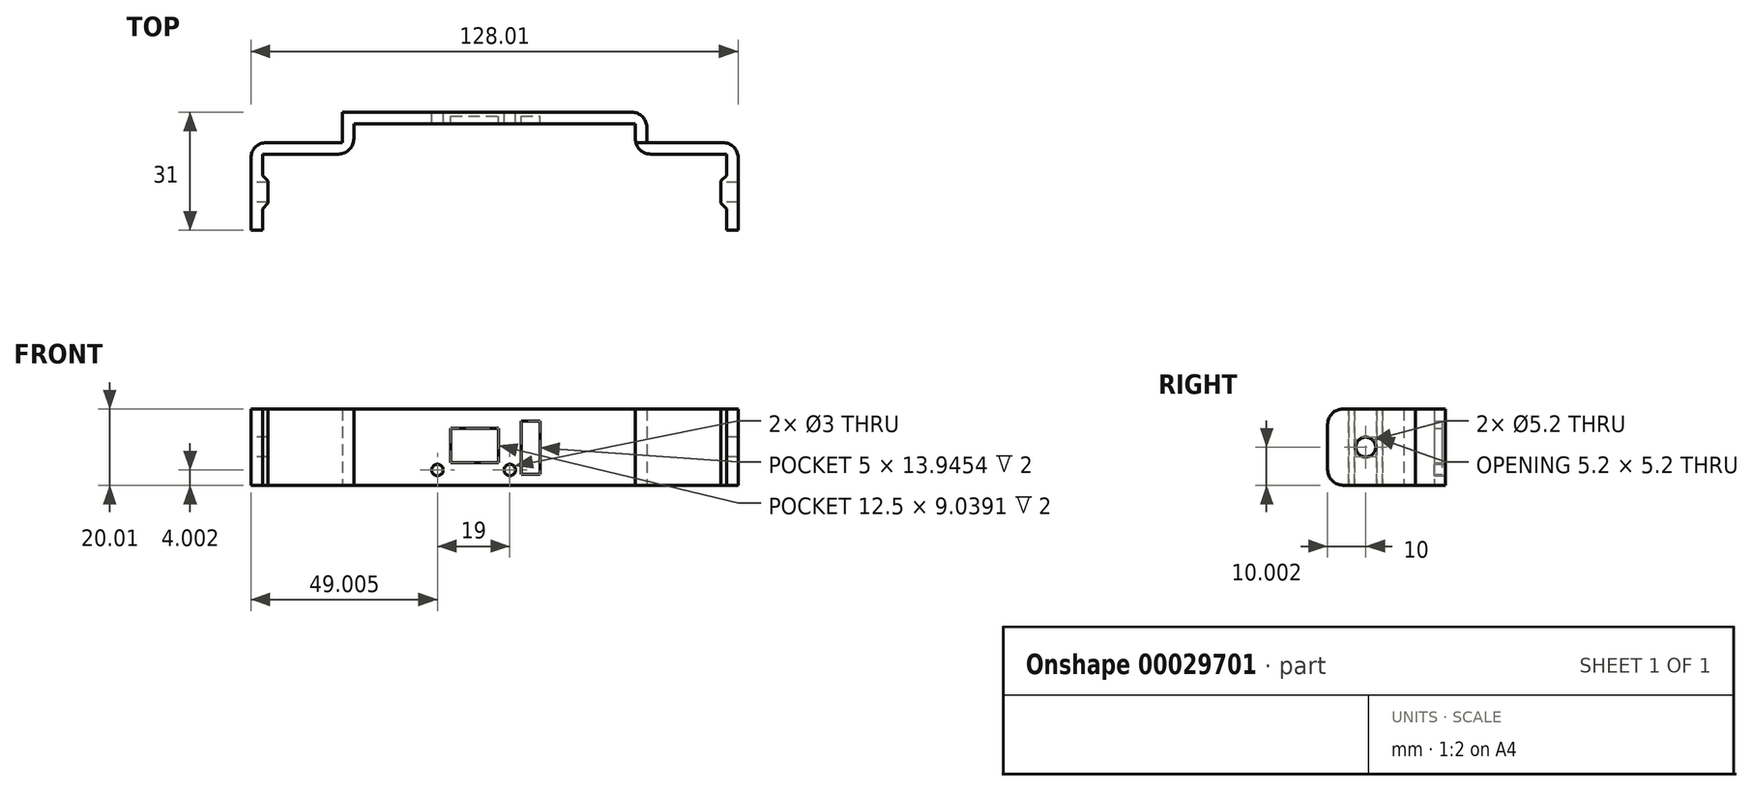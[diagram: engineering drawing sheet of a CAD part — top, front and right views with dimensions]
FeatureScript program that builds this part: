
annotation { "Feature Type Name" : "Feature", "Feature Type Description" : "" }
export const myFeature = defineFeature(function(context is Context, id is Id, definition is map)
    precondition{}
    {
        {
            var Q0;
            Q0=qCreatedBy(makeId("Front.planeOp"),FACE);
            var sketch = newSketch(context, id + "F0", { "sketchPlane" : qUnion([Q0])});
            skLineSegment(sketch, "E0.bottom", {"start": v(-55.19, 32.47) * mm, "end": v(24.81, 32.47) * mm});
            skLineSegment(sketch, "E0.top", {"start": v(-55.19, 12.47) * mm, "end": v(24.81, 12.47) * mm});
            skLineSegment(sketch, "E0.left", {"start": v(-55.19, 32.47) * mm, "end": v(-55.19, 12.47) * mm});
            skLineSegment(sketch, "E0.right", {"start": v(24.81, 32.47) * mm, "end": v(24.81, 12.47) * mm});
            skLineSegment(sketch, "E1.bottom", {"start": v(-26.69, 27.47) * mm, "end": v(-14.19, 27.47) * mm});
            skLineSegment(sketch, "E1.top", {"start": v(-26.69, 18.43) * mm, "end": v(-14.19, 18.43) * mm});
            skLineSegment(sketch, "E1.left", {"start": v(-26.69, 27.47) * mm, "end": v(-26.69, 18.43) * mm});
            skLineSegment(sketch, "E1.right", {"start": v(-14.19, 27.47) * mm, "end": v(-14.19, 18.43) * mm});
            skLineSegment(sketch, "E2.bottom", {"start": v(-8.19, 29.27) * mm, "end": v(-3.19, 29.27) * mm});
            skLineSegment(sketch, "E2.top", {"start": v(-8.19, 15.33) * mm, "end": v(-3.19, 15.33) * mm});
            skLineSegment(sketch, "E2.left", {"start": v(-8.19, 29.27) * mm, "end": v(-8.19, 15.33) * mm});
            skLineSegment(sketch, "E2.right", {"start": v(-3.19, 29.27) * mm, "end": v(-3.19, 15.33) * mm});
            skLineSegment(sketch, "E3.left", {"start": v(-55.19, 32.47) * mm, "end": v(-55.19, 29.47) * mm});
            skLineSegment(sketch, "E3.right", {"start": v(24.81, 32.47) * mm, "end": v(24.81, 29.47) * mm});
            skCircle(sketch, "E4", {"center": v(-30.19, 16.47) * mm, "radius": 1.5 * mm});
            skCircle(sketch, "E5", {"center": v(-11.19, 16.47) * mm, "radius": 1.5 * mm});
            skLineSegment(sketch, "E6.bottom", {"start": v(-55.19, 12.47) * mm, "end": v(-52.19, 12.47) * mm});
            skLineSegment(sketch, "E6.top", {"start": v(-55.19, 32.47) * mm, "end": v(-52.19, 32.47) * mm});
            skLineSegment(sketch, "E6.left", {"start": v(-55.19, 12.47) * mm, "end": v(-55.19, 32.47) * mm});
            skSolve(sketch);
        }
        {
            var Q0;
            Q0=makeQuery(id+"F0.imprint","IMPRINT",FACE,{"disambiguationData":[TD([[makeQuery(id+"F0.imprint","IMPRINT",EDGE,{"derivedFrom":sQuery(id+"F0.wireOp",EDGE,"E2.bottom")}),-1.0]])]});
            var Q1;
            Q1=makeQuery(id+"F0.imprint","IMPRINT",FACE,{"disambiguationData":[TD([[makeQuery(id+"F0.imprint","IMPRINT",EDGE,{"derivedFrom":sQuery(id+"F0.wireOp",EDGE,"E1.bottom")}),-1.0]])]});
            extrude(context, id + "F1", {"entities" : qUnion([Q0, Q1]), "depth" : 1 * mm});
        }
        {
            var Q0;
            Q0 = qSketchRegion(id + "F0", true);
            extrude(context, id + "F2", {"entities" : qUnion([Q0]), "operationType" : NewBodyOperationType.ADD, "depth" : 3 * mm});
        }
        {
            var Q0;
            Q0=makeQuery(id+"F2.opExtrude","CAP_FACE",FACE,{"disambiguationData":[OSD([sQuery(id+"F0.wireOp",EDGE,"E0.top"),sQuery(id+"F0.wireOp",EDGE,"E0.right"),sQuery(id+"F0.wireOp",EDGE,"E1.bottom"),sQuery(id+"F0.wireOp",EDGE,"E1.top"),sQuery(id+"F0.wireOp",EDGE,"E1.left"),sQuery(id+"F0.wireOp",EDGE,"E1.right"),sQuery(id+"F0.wireOp",EDGE,"E2.bottom"),sQuery(id+"F0.wireOp",EDGE,"E2.top"),sQuery(id+"F0.wireOp",EDGE,"E2.left"),sQuery(id+"F0.wireOp",EDGE,"E2.right"),sQuery(id+"F0.wireOp",EDGE,"E0.bottom"),sQuery(id+"F0.wireOp",EDGE,"E3.right"),sQuery(id+"F0.wireOp",EDGE,"E4"),sQuery(id+"F0.wireOp",EDGE,"E5"),sQuery(id+"F0.wireOp",EDGE,"E6.bottom"),sQuery(id+"F0.wireOp",EDGE,"E6.top"),sQuery(id+"F0.wireOp",EDGE,"E6.left")])],"isStart":false});
            var sketch = newSketch(context, id + "F3", { "sketchPlane" : qUnion([Q0])});
            skLineSegment(sketch, "E7.bottom", {"start": v(-55.19, 32.47) * mm, "end": v(-52.19, 32.47) * mm});
            skLineSegment(sketch, "E7.top", {"start": v(-55.19, 12.47) * mm, "end": v(-52.19, 12.47) * mm});
            skLineSegment(sketch, "E7.left", {"start": v(-55.19, 32.47) * mm, "end": v(-55.19, 12.47) * mm});
            skLineSegment(sketch, "E7.right", {"start": v(-52.19, 32.47) * mm, "end": v(-52.19, 12.47) * mm});
            skLineSegment(sketch, "E8.bottom", {"start": v(24.81, 32.47) * mm, "end": v(21.81, 32.47) * mm});
            skLineSegment(sketch, "E8.top", {"start": v(24.81, 12.47) * mm, "end": v(21.81, 12.47) * mm});
            skLineSegment(sketch, "E8.left", {"start": v(24.81, 32.47) * mm, "end": v(24.81, 12.47) * mm});
            skLineSegment(sketch, "E8.right", {"start": v(21.81, 32.47) * mm, "end": v(21.81, 12.47) * mm});
            skSolve(sketch);
        }
        {
            var Q0;
            Q0 = qSketchRegion(id + "F3", true);
            extrude(context, id + "F4", {"entities" : qUnion([Q0]), "operationType" : NewBodyOperationType.ADD, "depth" : 5 * mm});
        }
        {
            var Q0;
            Q0=makeQuery(id+"F4.opExtrude","CAP_FACE",FACE,{"disambiguationData":[OSD([sQuery(id+"F3.wireOp",EDGE,"E7.bottom"),sQuery(id+"F3.wireOp",EDGE,"E7.top"),sQuery(id+"F3.wireOp",EDGE,"E7.left"),sQuery(id+"F3.wireOp",EDGE,"E7.right")])],"isStart":false});
            var sketch = newSketch(context, id + "F5", { "sketchPlane" : qUnion([Q0])});
            skLineSegment(sketch, "E9.bottom", {"start": v(-52.19, 32.47) * mm, "end": v(-79.19, 32.47) * mm});
            skLineSegment(sketch, "E9.top", {"start": v(-52.19, 12.47) * mm, "end": v(-79.19, 12.47) * mm});
            skLineSegment(sketch, "E9.left", {"start": v(-52.19, 32.47) * mm, "end": v(-52.19, 12.47) * mm});
            skLineSegment(sketch, "E9.right", {"start": v(-79.19, 32.47) * mm, "end": v(-79.19, 12.47) * mm});
            skLineSegment(sketch, "E10.bottom", {"start": v(21.82, 32.48) * mm, "end": v(48.82, 32.48) * mm});
            skLineSegment(sketch, "E10.top", {"start": v(21.82, 12.47) * mm, "end": v(48.82, 12.47) * mm});
            skLineSegment(sketch, "E10.left", {"start": v(21.82, 32.48) * mm, "end": v(21.82, 12.47) * mm});
            skLineSegment(sketch, "E10.right", {"start": v(48.82, 32.48) * mm, "end": v(48.82, 12.47) * mm});
            skSolve(sketch);
        }
        {
            var Q0;
            Q0 = qSketchRegion(id + "F5", true);
            extrude(context, id + "F6", {"entities" : qUnion([Q0]), "operationType" : NewBodyOperationType.ADD, "depth" : 3 * mm});
        }
        {
            var Q0;
            Q0=makeQuery(id+"F6.opExtrude","CAP_FACE",FACE,{"disambiguationData":[OSD([sQuery(id+"F5.wireOp",EDGE,"E9.bottom"),sQuery(id+"F5.wireOp",EDGE,"E9.top"),sQuery(id+"F5.wireOp",EDGE,"E9.left"),sQuery(id+"F5.wireOp",EDGE,"E9.right")])],"isStart":false});
            var sketch = newSketch(context, id + "F7", { "sketchPlane" : qUnion([Q0])});
            skLineSegment(sketch, "E11.bottom", {"start": v(-79.19, 32.47) * mm, "end": v(-76.19, 32.47) * mm});
            skLineSegment(sketch, "E11.top", {"start": v(-79.19, 12.47) * mm, "end": v(-76.19, 12.47) * mm});
            skLineSegment(sketch, "E11.left", {"start": v(-79.19, 32.47) * mm, "end": v(-79.19, 12.47) * mm});
            skLineSegment(sketch, "E11.right", {"start": v(-76.19, 32.47) * mm, "end": v(-76.19, 12.47) * mm});
            skSolve(sketch);
        }
        {
            var Q0;
            Q0 = qSketchRegion(id + "F7", true);
            extrude(context, id + "F8", {"entities" : qUnion([Q0]), "operationType" : NewBodyOperationType.ADD, "depth" : 20 * mm});
        }
        {
            var Q0;
            Q0=makeQuery(id+"F6.opExtrude","CAP_FACE",FACE,{"disambiguationData":[OSD([sQuery(id+"F5.wireOp",EDGE,"E10.bottom"),sQuery(id+"F5.wireOp",EDGE,"E10.top"),sQuery(id+"F5.wireOp",EDGE,"E10.left"),sQuery(id+"F5.wireOp",EDGE,"E10.right")])],"isStart":false});
            var sketch = newSketch(context, id + "F9", { "sketchPlane" : qUnion([Q0])});
            skLineSegment(sketch, "E12.bottom", {"start": v(48.82, 32.48) * mm, "end": v(45.82, 32.48) * mm});
            skLineSegment(sketch, "E12.top", {"start": v(48.82, 12.47) * mm, "end": v(45.82, 12.47) * mm});
            skLineSegment(sketch, "E12.left", {"start": v(48.82, 32.48) * mm, "end": v(48.82, 12.47) * mm});
            skLineSegment(sketch, "E12.right", {"start": v(45.82, 32.48) * mm, "end": v(45.82, 12.47) * mm});
            skSolve(sketch);
        }
        {
            var Q0;
            Q0 = qSketchRegion(id + "F9", true);
            extrude(context, id + "F10", {"entities" : qUnion([Q0]), "operationType" : NewBodyOperationType.ADD, "depth" : 20 * mm});
        }
        {
            var Q0;
            Q0=makeQuery(id+"F10.opExtrude","SWEPT_FACE",FACE,{"disambiguationData":[OSD([sQuery(id+"F9.wireOp",EDGE,"E12.right")])]});
            var sketch = newSketch(context, id + "F11", { "sketchPlane" : qUnion([Q0])});
            skLineSegment(sketch, "E13.bottom", {"start": v(25.4, 32.48) * mm, "end": v(16.6, 32.48) * mm});
            skLineSegment(sketch, "E13.top", {"start": v(25.4, 12.47) * mm, "end": v(16.6, 12.47) * mm});
            skLineSegment(sketch, "E13.left", {"start": v(25.4, 32.48) * mm, "end": v(25.4, 12.47) * mm});
            skLineSegment(sketch, "E13.right", {"start": v(16.6, 32.48) * mm, "end": v(16.6, 12.47) * mm});
            skSolve(sketch);
        }
        {
            var Q0;
            Q0=makeQuery(id+"F8.opExtrude","SWEPT_FACE",FACE,{"disambiguationData":[OSD([sQuery(id+"F7.wireOp",EDGE,"E11.right")])]});
            var sketch = newSketch(context, id + "F12", { "sketchPlane" : qUnion([Q0])});
            skLineSegment(sketch, "E14.bottom", {"start": v(-25.4, 12.47) * mm, "end": v(-16.6, 12.47) * mm});
            skLineSegment(sketch, "E14.top", {"start": v(-25.4, 32.47) * mm, "end": v(-16.6, 32.47) * mm});
            skLineSegment(sketch, "E14.left", {"start": v(-25.4, 12.47) * mm, "end": v(-25.4, 32.47) * mm});
            skLineSegment(sketch, "E14.right", {"start": v(-16.6, 12.47) * mm, "end": v(-16.6, 32.47) * mm});
            skSolve(sketch);
        }
        {
            var Q0;
            Q0 = qSketchRegion(id + "F12", true);
            extrude(context, id + "F13", {"entities" : qUnion([Q0]), "operationType" : NewBodyOperationType.ADD, "depth" : 1.5 * mm});
        }
        {
            var Q0;
            Q0 = qSketchRegion(id + "F11", true);
            extrude(context, id + "F14", {"entities" : qUnion([Q0]), "operationType" : NewBodyOperationType.ADD, "depth" : 1.5 * mm});
        }
        {
            var Q0;
            Q0=makeQuery(id+"F8.boolean.opBoolean","MERGE",FACE,{"derivedFrom":[makeQuery(id+"F6.opExtrude","SWEPT_FACE",FACE,{"disambiguationData":[OSD([sQuery(id+"F5.wireOp",EDGE,"E9.right")])]}),makeQuery(id+"F8.opExtrude","SWEPT_FACE",FACE,{"disambiguationData":[OSD([sQuery(id+"F7.wireOp",EDGE,"E11.left")])]})]});
            var sketch = newSketch(context, id + "F15", { "sketchPlane" : qUnion([Q0])});
            skCircle(sketch, "E15", {"center": v(21, 22.47) * mm, "radius": 2.6 * mm});
            skSolve(sketch);
        }
        {
            var Q0;
            Q0=makeQuery(id+"F15.imprint","IMPRINT",FACE,{"disambiguationData":[TD([[makeQuery(id+"F15.imprint","IMPRINT",EDGE,{"derivedFrom":sQuery(id+"F15.wireOp",EDGE,"E15")}),1.0]])]});
            extrude(context, id + "F16", {"entities" : qUnion([Q0]), "operationType" : NewBodyOperationType.REMOVE, "endBound" : BoundingType.THROUGH_ALL, "oppositeDirection" : true, "depth" : 25 * mm});
        }
        {
            var Q0;
            Q0=makeQuery(id+"F8.opExtrude","CAP_EDGE",EDGE,{"disambiguationData":[OSD([sQuery(id+"F7.wireOp",EDGE,"E11.bottom")])],"isStart":false});
            var Q1;
            Q1=makeQuery(id+"F10.opExtrude","CAP_EDGE",EDGE,{"disambiguationData":[OSD([sQuery(id+"F9.wireOp",EDGE,"E12.bottom")])],"isStart":false});
            var Q2;
            Q2=makeQuery(id+"F8.opExtrude","CAP_EDGE",EDGE,{"disambiguationData":[OSD([sQuery(id+"F7.wireOp",EDGE,"E11.top")])],"isStart":false});
            var Q3;
            Q3=makeQuery(id+"F10.opExtrude","CAP_EDGE",EDGE,{"disambiguationData":[OSD([sQuery(id+"F9.wireOp",EDGE,"E12.top")])],"isStart":false});
            var Q4;
            Q4=makeQuery(id+"F4.opExtrude","CAP_EDGE",EDGE,{"disambiguationData":[OSD([sQuery(id+"F3.wireOp",EDGE,"E8.right")])],"isStart":true});
            var Q5;
            Q5=makeQuery(id+"F4.opExtrude","CAP_EDGE",EDGE,{"disambiguationData":[OSD([sQuery(id+"F3.wireOp",EDGE,"E7.right")])],"isStart":true});
            var Q6;
            Q6=makeQuery(id+"F2.opExtrude","CAP_EDGE",EDGE,{"disambiguationData":[OSD([sQuery(id+"F0.wireOp",EDGE,"E6.left")])],"isStart":true});
            var Q7;
            Q7=makeQuery(id+"F2.opExtrude","CAP_EDGE",EDGE,{"disambiguationData":[OSD([sQuery(id+"F0.wireOp",EDGE,"E0.right"),sQuery(id+"F0.wireOp",EDGE,"E3.right")])],"isStart":true});
            var Q8;
            Q8=makeQuery(id+"F6.opExtrude","CAP_EDGE",EDGE,{"disambiguationData":[OSD([sQuery(id+"F5.wireOp",EDGE,"E10.left")])],"isStart":false});
            var Q9;
            Q9=makeQuery(id+"F4.opExtrude","CAP_EDGE",EDGE,{"disambiguationData":[OSD([sQuery(id+"F3.wireOp",EDGE,"E8.left")])],"isStart":false});
            var Q10;
            Q10=makeQuery(id+"F6.opExtrude","CAP_EDGE",EDGE,{"disambiguationData":[OSD([sQuery(id+"F5.wireOp",EDGE,"E10.right")])],"isStart":true});
            var Q11;
            Q11=makeQuery(id+"F4.opExtrude","CAP_EDGE",EDGE,{"disambiguationData":[OSD([sQuery(id+"F3.wireOp",EDGE,"E7.left")])],"isStart":false});
            var Q12;
            Q12=makeQuery(id+"F6.opExtrude","CAP_EDGE",EDGE,{"disambiguationData":[OSD([sQuery(id+"F5.wireOp",EDGE,"E9.right")])],"isStart":true});
            var Q13;
            Q13=makeQuery(id+"F6.opExtrude","CAP_EDGE",EDGE,{"disambiguationData":[OSD([sQuery(id+"F5.wireOp",EDGE,"E9.left")])],"isStart":false});
            fillet(context, id + "F17", {"entities" : qUnion([Q0, Q1, Q2, Q3, Q4, Q5, Q6, Q7, Q8, Q9, Q10, Q11, Q12, Q13]), "radius" : 4 * mm, "tangentPropagation" : true, "allowEdgeOverflow" : false});
        }
        {
            var Q0;
            Q0=makeQuery(id+"F14.opExtrude","CAP_EDGE",EDGE,{"disambiguationData":[OSD([sQuery(id+"F11.wireOp",EDGE,"E13.left")])],"isStart":false});
            var Q1;
            Q1=makeQuery(id+"F14.opExtrude","CAP_EDGE",EDGE,{"disambiguationData":[OSD([sQuery(id+"F11.wireOp",EDGE,"E13.right")])],"isStart":false});
            var Q2;
            Q2=makeQuery(id+"F13.opExtrude","CAP_EDGE",EDGE,{"disambiguationData":[OSD([sQuery(id+"F12.wireOp",EDGE,"E14.left")])],"isStart":false});
            var Q3;
            Q3=makeQuery(id+"F13.opExtrude","CAP_EDGE",EDGE,{"disambiguationData":[OSD([sQuery(id+"F12.wireOp",EDGE,"E14.right")])],"isStart":false});
            chamfer(context, id + "F18", {"entities" : qUnion([Q0, Q1, Q2, Q3]), "width" : 1.5 * mm, "tangentPropagation" : true});
        }
    });
